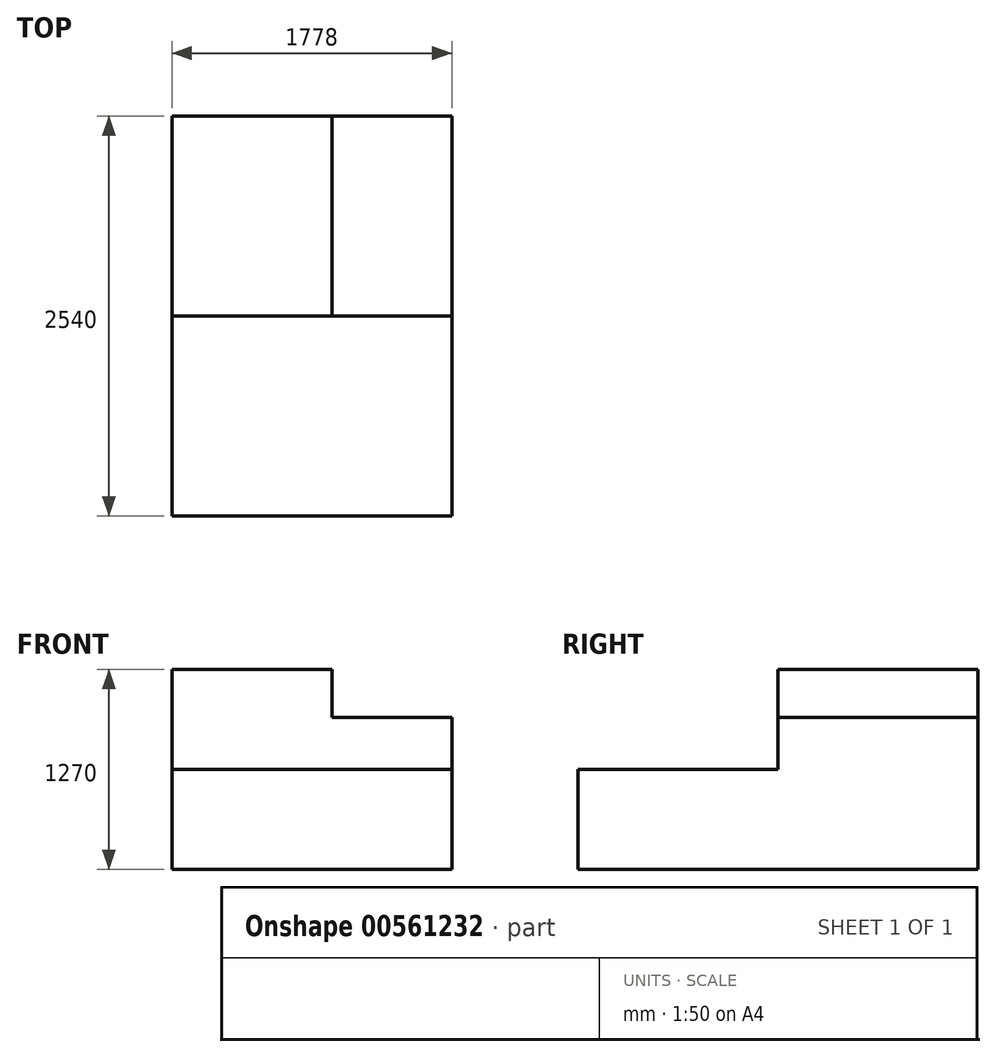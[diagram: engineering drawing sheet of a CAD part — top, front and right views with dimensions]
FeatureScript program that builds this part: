
annotation { "Feature Type Name" : "Feature", "Feature Type Description" : "" }
export const myFeature = defineFeature(function(context is Context, id is Id, definition is map)
    precondition{}
    {
        {
            var Q0;
            Q0=qCreatedBy(makeId("Front.planeOp"),FACE);
            var sketch = newSketch(context, id + "F0", { "sketchPlane" : qUnion([Q0])});
            skLineSegment(sketch, "E0.bottom", {"start": v(-786, -354.24) * mm, "end": v(992, -354.24) * mm});
            skLineSegment(sketch, "E0.top", {"start": v(-786, 280.76) * mm, "end": v(992, 280.76) * mm});
            skLineSegment(sketch, "E0.left", {"start": v(-786, -354.24) * mm, "end": v(-786, 280.76) * mm});
            skLineSegment(sketch, "E0.right", {"start": v(992, -354.24) * mm, "end": v(992, 280.76) * mm});
            skSolve(sketch);
        }
        {
            var Q0;
            Q0=makeQuery(id+"F0.imprint","IMPRINT",FACE,{"disambiguationData":[TD([[makeQuery(id+"F0.imprint","IMPRINT",EDGE,{"derivedFrom":sQuery(id+"F0.wireOp",EDGE,"E0.bottom")}),1.0]])]});
            extrude(context, id + "F1", {"entities" : qUnion([Q0]), "depth" : 2540 * mm, "offsetDistance" : 25.4 * mm});
        }
        {
            var Q0;
            Q0=makeQuery(id+"F1.opExtrude","SWEPT_FACE",FACE,{"disambiguationData":[OSD([sQuery(id+"F0.wireOp",EDGE,"E0.top")])]});
            var sketch = newSketch(context, id + "F2", { "sketchPlane" : qUnion([Q0])});
            skLineSegment(sketch, "E1", {"start": v(-786, -1270) * mm, "end": v(992, -1270) * mm});
            skLineSegment(sketch, "E2", {"start": v(-786, 0) * mm, "end": v(230, 0) * mm});
            skLineSegment(sketch, "E3", {"start": v(230, 0) * mm, "end": v(230, -1270) * mm});
            skSolve(sketch);
        }
        {
            var Q0;
            {var subQ4=sQuery(id+"F2.wireOp",EDGE,"E3");Q0=makeQuery(id+"F2.imprint","IMPRINT",FACE,{"disambiguationData":[TD([[makeQuery(id+"F2.imprint","IMPRINT",EDGE,{"derivedFrom":subQ4}),1.0]])]});}
            extrude(context, id + "F3", {"entities" : qUnion([Q0]), "operationType" : NewBodyOperationType.ADD, "depth" : 330.2 * mm, "offsetDistance" : 25.4 * mm});
        }
        {
            var Q0;
            {var subQ4=sQuery(id+"F2.wireOp",EDGE,"E2");Q0=makeQuery(id+"F2.imprint","IMPRINT",FACE,{"disambiguationData":[TD([[makeQuery(id+"F2.imprint","IMPRINT",EDGE,{"derivedFrom":subQ4}),-1.0]])]});}
            extrude(context, id + "F4", {"entities" : qUnion([Q0]), "operationType" : NewBodyOperationType.ADD, "depth" : 635 * mm, "offsetDistance" : 25.4 * mm});
        }
    });
